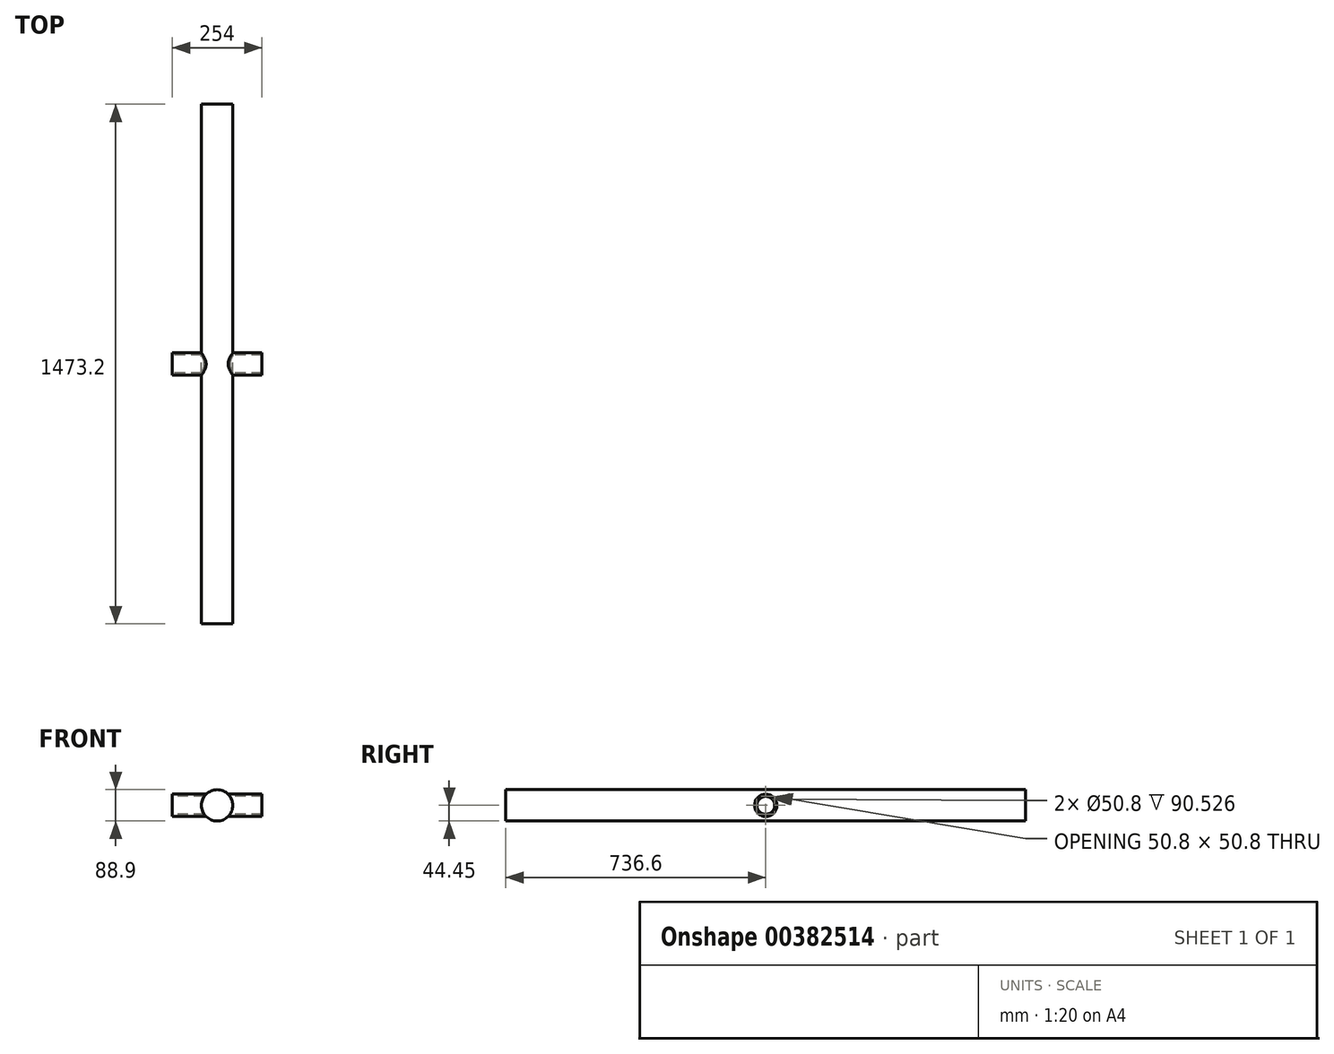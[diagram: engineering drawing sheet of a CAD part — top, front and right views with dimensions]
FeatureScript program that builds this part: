
annotation { "Feature Type Name" : "Feature", "Feature Type Description" : "" }
export const myFeature = defineFeature(function(context is Context, id is Id, definition is map)
    precondition{}
    {
        {
            var Q0;
            Q0=qCreatedBy(makeId("Front.planeOp"),FACE);
            var sketch = newSketch(context, id + "F0", { "sketchPlane" : qUnion([Q0])});
            skCircle(sketch, "E0", {"center": v(0, 0) * mm, "radius": 44.45 * mm});
            skSolve(sketch);
        }
        {
            var Q0;
            Q0 = qSketchRegion(id + "F0", true);
            extrude(context, id + "F1", {"entities" : qUnion([Q0]), "depth" : 25.4 * mm});
        }
        {
            var Q0;
            Q0 = qSketchRegion(id + "F0", true);
            extrude(context, id + "F2", {"entities" : qUnion([Q0]), "operationType" : NewBodyOperationType.ADD, "depth" : 1473.2 * mm});
        }
        {
            var Q0;
            Q0=qCreatedBy(makeId("Right.planeOp"),FACE);
            var sketch = newSketch(context, id + "F3", { "sketchPlane" : qUnion([Q0])});
            skCircle(sketch, "E1", {"center": v(-736.6, 0) * mm, "radius": 25.4 * mm});
            skCircle(sketch, "E2.0", {"center": v(-736.6, 0) * mm, "radius": 31.75 * mm});
            skSolve(sketch);
        }
        {
            var Q0;
            Q0 = qSketchRegion(id + "F3", true);
            extrude(context, id + "F4", {"entities" : qUnion([Q0]), "operationType" : NewBodyOperationType.ADD, "depth" : 127 * mm, "hasSecondDirection" : true, "secondDirectionOppositeDirection" : true, "secondDirectionDepth" : 127 * mm});
        }
    });
